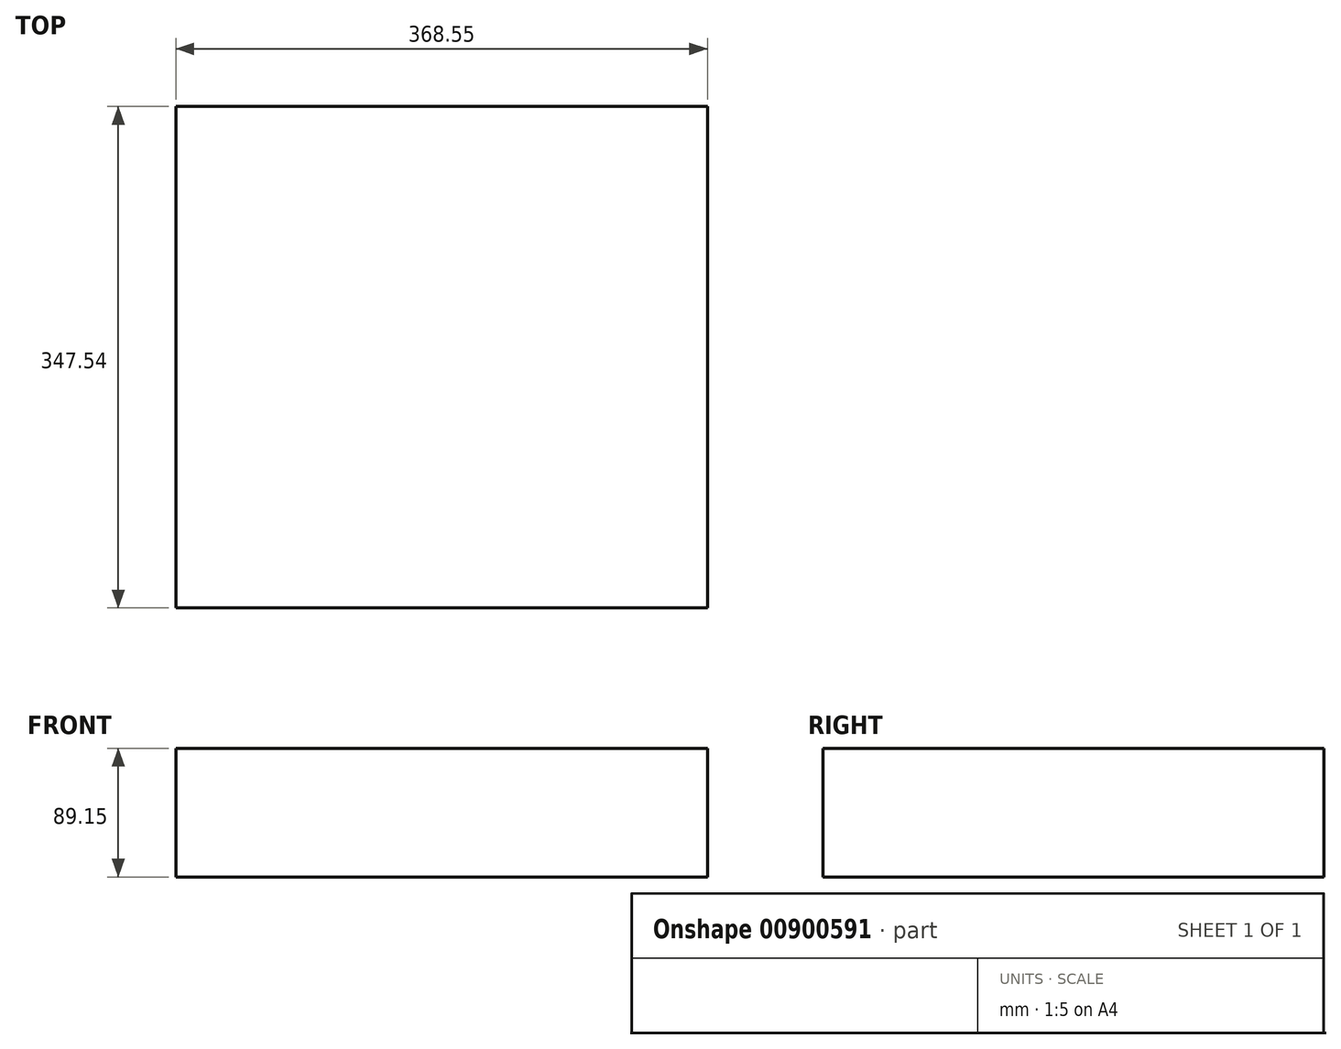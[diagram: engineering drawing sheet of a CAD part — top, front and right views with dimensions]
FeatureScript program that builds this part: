
annotation { "Feature Type Name" : "Feature", "Feature Type Description" : "" }
export const myFeature = defineFeature(function(context is Context, id is Id, definition is map)
    precondition{}
    {
        {
            var Q0;
            Q0=qCreatedBy(makeId("Top.planeOp"),FACE);
            var sketch = newSketch(context, id + "F0", { "sketchPlane" : qUnion([Q0])});
            skLineSegment(sketch, "E0", {"start": v(-37.11, -57.32) * mm, "end": v(0, 39.85) * mm});
            skLineSegment(sketch, "E1", {"start": v(0, 39.85) * mm, "end": v(-42.06, 72.91) * mm});
            skLineSegment(sketch, "E2", {"start": v(-42.06, 72.91) * mm, "end": v(-42.06, 105.79) * mm});
            skSolve(sketch);
        }
        {
            var Q0;
            Q0=sQuery(id+"F0.wireOp",VERTEX,"E0.start");
            var Q1;
            Q1=sQuery(id+"F0.wireOp",EDGE,"E0");
            cPlane(context, id + "F1", {"entities" : qUnion([Q0, Q1]), "cplaneType" : CPlaneType.LINE_POINT, "offset" : 25.4 * mm, "width" : 152.4 * mm, "height" : 152.4 * mm});
        }
        {
            var Q0;
            Q0=qCreatedBy(id+"F1.planeOp",FACE);
            var sketch = newSketch(context, id + "F2", { "sketchPlane" : qUnion([Q0])});
            skLineSegment(sketch, "E3.bottom", {"start": v(0, 0) * mm, "end": v(-34.5, 0) * mm});
            skLineSegment(sketch, "E3.top", {"start": v(0, 39.97) * mm, "end": v(-34.5, 39.97) * mm});
            skLineSegment(sketch, "E3.left", {"start": v(0, 0) * mm, "end": v(0, 39.97) * mm});
            skLineSegment(sketch, "E3.right", {"start": v(-34.5, 0) * mm, "end": v(-34.5, 39.97) * mm});
            skSolve(sketch);
        }
        {
            var Q0;
            Q0=makeQuery(id+"F2.imprint","IMPRINT",FACE,{"disambiguationData":[TD([[makeQuery(id+"F2.imprint","IMPRINT",EDGE,{"derivedFrom":sQuery(id+"F2.wireOp",EDGE,"E3.bottom")}),-1.0]])]});
            var Q1;
            Q1=sQuery(id+"F0.wireOp",EDGE,"E1");
            var Q2;
            Q2=sQuery(id+"F0.wireOp",EDGE,"E2");
            var Q3;
            Q3=sQuery(id+"F0.wireOp",EDGE,"E0");
            sweep(context, id + "F3", {"profiles" : qUnion([Q0]), "path" : qUnion([Q1, Q2, Q3])});
        }
        {
            var Q0;
            Q0=makeQuery(id+"F3.opSweep","SWEPT_FACE",FACE,{"disambiguationData":[OSD([sQuery(id+"F0.wireOp",EDGE,"E0"),sQuery(id+"F2.wireOp",EDGE,"E3.left")])]});
            var sketch = newSketch(context, id + "F4", { "sketchPlane" : qUnion([Q0])});
            skLineSegment(sketch, "E4", {"start": v(0, 15.36) * mm, "end": v(36.22, 39.97) * mm});
            skLineSegment(sketch, "E5", {"start": v(36.22, 39.97) * mm, "end": v(59.62, 55.87) * mm});
            skSolve(sketch);
        }
        {
            var Q0;
            Q0=sQuery(id+"F4.wireOp",VERTEX,"E4.end");
            var Q1;
            Q1=sQuery(id+"F4.wireOp",EDGE,"E4");
            cPlane(context, id + "F5", {"entities" : qUnion([Q0, Q1]), "cplaneType" : CPlaneType.LINE_POINT, "offset" : 25.4 * mm, "width" : 152.4 * mm, "height" : 152.4 * mm});
        }
        {
            var Q0;
            Q0=qCreatedBy(id+"F5.planeOp",FACE);
            var sketch = newSketch(context, id + "F6", { "sketchPlane" : qUnion([Q0])});
            skCircle(sketch, "E6", {"center": v(10.33, 12.55) * mm, "radius": 9.17 * mm});
            skSolve(sketch);
        }
        {
            var Q0;
            Q0=makeQuery(id+"F6.imprint","IMPRINT",FACE,{"disambiguationData":[TD([[makeQuery(id+"F6.imprint","IMPRINT",EDGE,{"derivedFrom":sQuery(id+"F6.wireOp",EDGE,"E6")}),1.0]])]});
            var Q1;
            Q1=sQuery(id+"F4.wireOp",EDGE,"E4");
            var Q2;
            Q2=sQuery(id+"F4.wireOp",EDGE,"E5");
            sweep(context, id + "F7", {"operationType" : NewBodyOperationType.REMOVE, "profiles" : qUnion([Q0]), "path" : qUnion([Q1, Q2])});
        }
        {
            var Q0;
            Q0=qCreatedBy(makeId("Top.planeOp"),FACE);
            var sketch = newSketch(context, id + "F8", { "sketchPlane" : qUnion([Q0])});
            skLineSegment(sketch, "E7.bottom", {"start": v(-170.33, 161.58) * mm, "end": v(198.22, 161.58) * mm});
            skLineSegment(sketch, "E7.top", {"start": v(-170.33, -185.96) * mm, "end": v(198.22, -185.96) * mm});
            skLineSegment(sketch, "E7.left", {"start": v(-170.33, 161.58) * mm, "end": v(-170.33, -185.96) * mm});
            skLineSegment(sketch, "E7.right", {"start": v(198.22, 161.58) * mm, "end": v(198.22, -185.96) * mm});
            skSolve(sketch);
        }
        {
            var Q0;
            Q0=makeQuery(id+"F8.imprint","IMPRINT",FACE,{"disambiguationData":[TD([[makeQuery(id+"F8.imprint","IMPRINT",EDGE,{"derivedFrom":sQuery(id+"F8.wireOp",EDGE,"E7.bottom")}),-1.0]])]});
            extrude(context, id + "F9", {"entities" : qUnion([Q0]), "operationType" : NewBodyOperationType.ADD, "depth" : 89.15 * mm, "offsetDistance" : 25.4 * mm});
        }
    });
